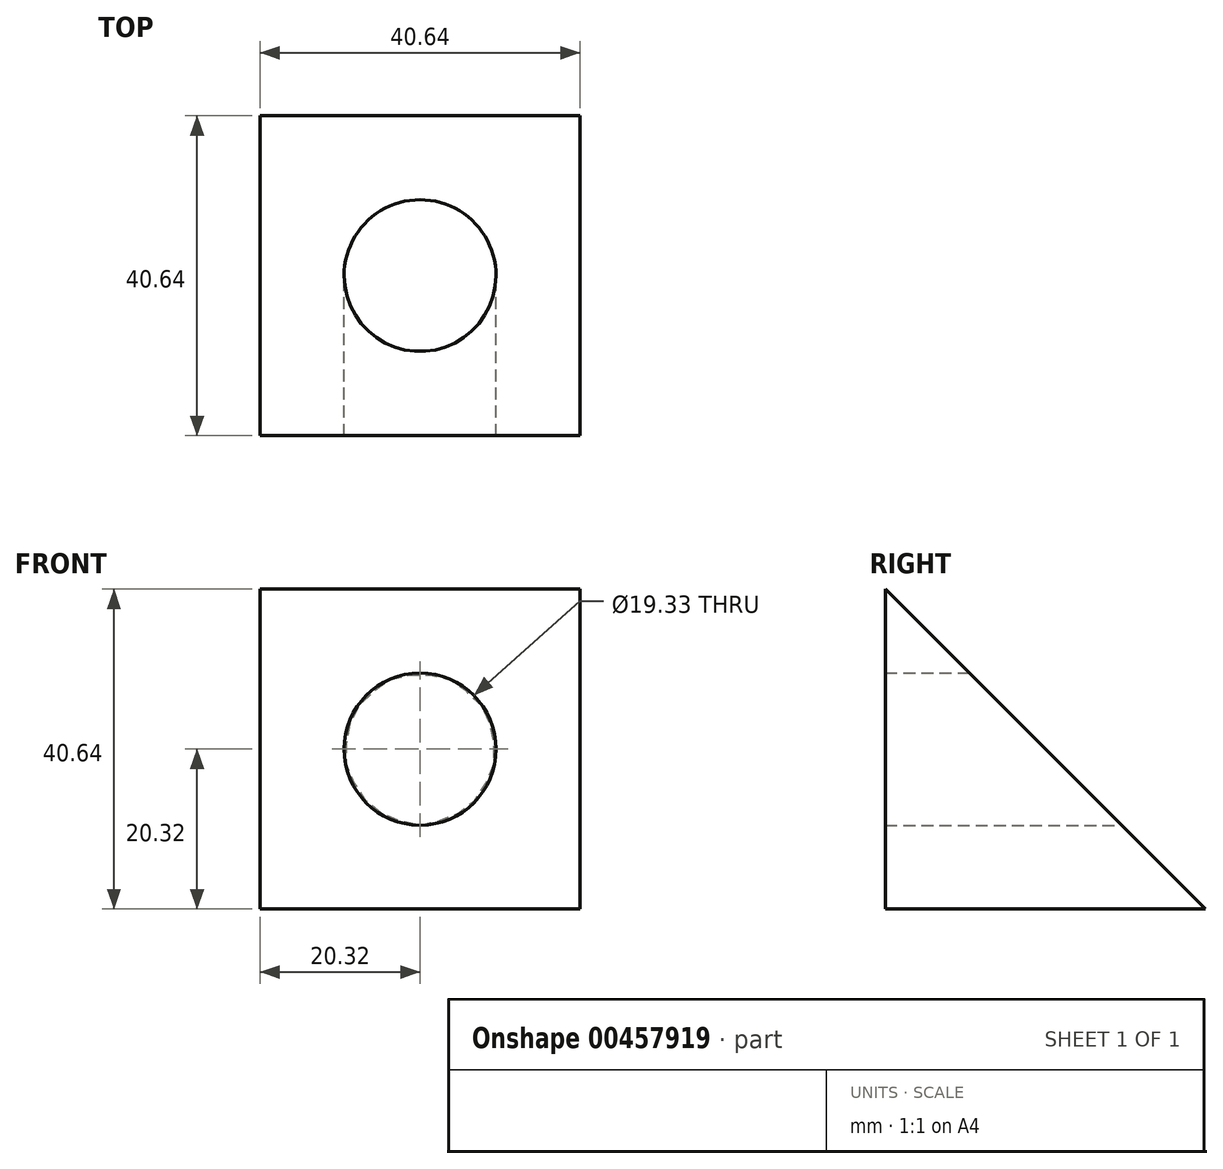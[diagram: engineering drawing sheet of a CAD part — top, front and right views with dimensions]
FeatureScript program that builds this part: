
annotation { "Feature Type Name" : "Feature", "Feature Type Description" : "" }
export const myFeature = defineFeature(function(context is Context, id is Id, definition is map)
    precondition{}
    {
        {
            var Q0;
            Q0=qCreatedBy(makeId("Front.planeOp"),FACE);
            var sketch = newSketch(context, id + "F0", { "sketchPlane" : qUnion([Q0])});
            skLineSegment(sketch, "E0.bottom", {"start": v(0, 0) * mm, "end": v(-40.64, 0) * mm});
            skLineSegment(sketch, "E0.top", {"start": v(0, 40.64) * mm, "end": v(-40.64, 40.64) * mm});
            skLineSegment(sketch, "E0.left", {"start": v(0, 0) * mm, "end": v(0, 40.64) * mm});
            skLineSegment(sketch, "E0.right", {"start": v(-40.64, 0) * mm, "end": v(-40.64, 40.64) * mm});
            skLineSegment(sketch, "E1", {"start": v(-20.32, 40.64) * mm, "end": v(-20.32, 0) * mm, "construction": true});
            skCircle(sketch, "E2", {"center": v(-20.32, 20.32) * mm, "radius": 9.65 * mm, "construction": true});
            skCircle(sketch, "E3", {"center": v(-20.32, 20.32) * mm, "radius": 9.67 * mm});
            skSolve(sketch);
        }
        {
            var Q0;
            Q0=qSketchRegion(id+"F0",true);
            extrude(context, id + "F1", {"entities" : qUnion([Q0]), "depth" : 40.64 * mm});
        }
        {
            var Q0;
            Q0=makeQuery(id+"F1.opExtrude","SWEPT_FACE",FACE,{"disambiguationData":[OSD([sQuery(id+"F0.wireOp",EDGE,"E0.left")])]});
            var sketch = newSketch(context, id + "F2", { "sketchPlane" : qUnion([Q0])});
            skLineSegment(sketch, "E4", {"start": v(-40.64, 40.64) * mm, "end": v(0, 0) * mm});
            skSolve(sketch);
        }
        {
            var Q0;
            Q0=makeQuery(id+"F2.imprint","IMPRINT",FACE,{"disambiguationData":[TD([[makeQuery(id+"F2.imprint","IMPRINT",EDGE,{"derivedFrom":sQuery(id+"F2.wireOp",EDGE,"E4")}),1.0]])]});
            extrude(context, id + "F3", {"entities" : qUnion([Q0]), "operationType" : NewBodyOperationType.REMOVE, "endBound" : BoundingType.THROUGH_ALL, "oppositeDirection" : true, "depth" : 25.4 * mm});
        }
    });
